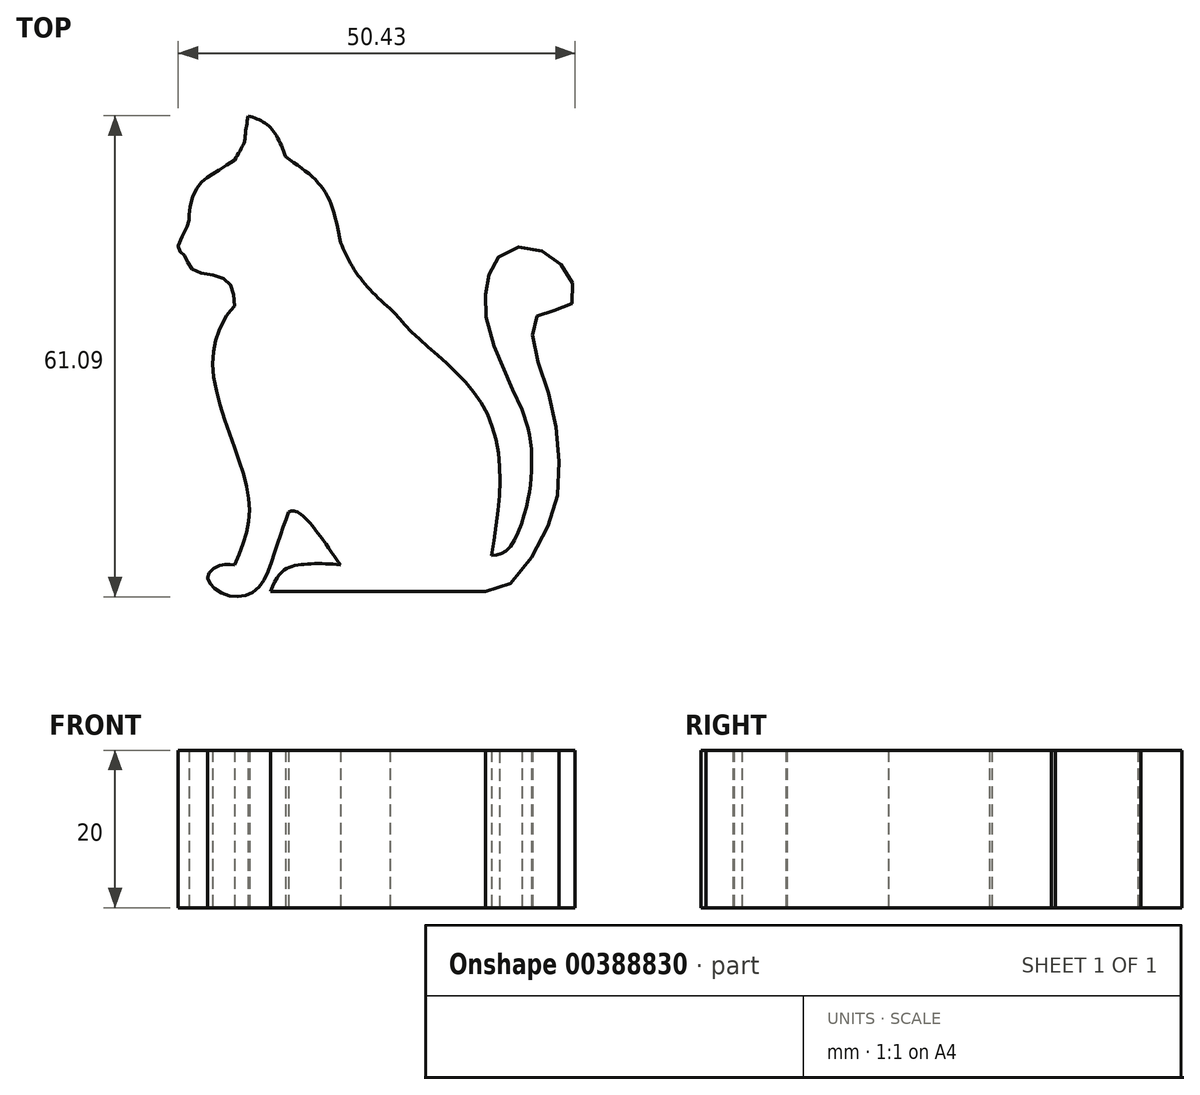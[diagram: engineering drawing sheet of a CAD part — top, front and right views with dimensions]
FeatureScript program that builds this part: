
annotation { "Feature Type Name" : "Feature", "Feature Type Description" : "" }
export const myFeature = defineFeature(function(context is Context, id is Id, definition is map)
    precondition{}
    {
        {
            var Q0;
            Q0=qCreatedBy(makeId("Top.planeOp"),FACE);
            var sketch = newSketch(context, id + "F0", { "sketchPlane" : qUnion([Q0])});
            skFitSpline(sketch, "E0", {"points": [v(-17.16, 28.37) * mm, v(-17.53, 25.84) * mm, v(-17.62, 25.13) * mm, v(-18.9, 22.75) * mm], "startDerivative": vector(-1.28, -7.63) * mm, "endDerivative": vector(-4.15, -6.95) * mm});
            skFitSpline(sketch, "E1", {"points": [v(-18.9, 22.75) * mm, v(-21.25, 21.24) * mm, v(-22.64, 20.3) * mm, v(-24.03, 18.5) * mm, v(-24.68, 15.66) * mm, v(-24.8, 14.64) * mm, v(-26.05, 11.46) * mm, v(-25.25, 10.67) * mm, v(-24.23, 8.85) * mm, v(-20.03, 7.6) * mm, v(-18.9, 4.2) * mm], "startDerivative": vector(-23.37, -15.12) * mm, "endDerivative": vector(1.87, -33.89) * mm});
            skFitSpline(sketch, "E2", {"points": [v(-18.9, 4.2) * mm, v(-20.2, 2.45) * mm, v(-21.65, -3.17) * mm, v(-18.9, -13.76) * mm, v(-17, -22.1) * mm, v(-18.9, -28.7) * mm], "startDerivative": vector(-11.23, -12.61) * mm, "endDerivative": vector(-13.18, -31.36) * mm});
            skFitSpline(sketch, "E3", {"points": [v(-18.9, -28.7) * mm, v(-20.53, -28.7) * mm, v(-22.3, -30.14) * mm, v(-20.2, -32.38) * mm, v(-16.2, -31.9) * mm, v(-13.62, -26.54) * mm, v(-12.02, -21.95) * mm], "startDerivative": vector(-13.16, 2.23) * mm, "endDerivative": vector(8.03, 21.7) * mm});
            skFitSpline(sketch, "E4", {"points": [v(-12.02, -21.95) * mm, v(-10.9, -21.95) * mm, v(-5.44, -28.7) * mm], "startDerivative": vector(3.83, 1.21) * mm, "endDerivative": vector(8.6, -12.54) * mm});
            skFitSpline(sketch, "E5", {"points": [v(-5.44, -28.7) * mm, v(-10.73, -28.7) * mm, v(-14.34, -32.08) * mm], "startDerivative": vector(-10.81, 1.41) * mm, "endDerivative": vector(-6.33, -16.88) * mm});
            skLineSegment(sketch, "E6", {"start": v(-14.34, -32.08) * mm, "end": v(13.02, -32.08) * mm});
            skFitSpline(sketch, "E7", {"points": [v(13.02, -32.08) * mm, v(16.43, -30.83) * mm, v(20.08, -25.5) * mm, v(22.03, -20.3) * mm, v(22.24, -14.16) * mm, v(21.3, -7.88) * mm, v(19.47, -2.34) * mm, v(18.95, 1.15) * mm, v(19.57, 2.92) * mm, v(21.05, 3.54) * mm, v(23.05, 3.92) * mm, v(24.34, 5.2) * mm, v(23.72, 7.83) * mm, v(22.33, 9.74) * mm, v(19.76, 11.36) * mm, v(16.85, 11.65) * mm, v(14.5, 10.31) * mm, v(13.55, 8.45) * mm, v(13.02, 6.54) * mm, v(13.02, 3.63) * mm, v(13.4, 0.86) * mm, v(17.13, -7.96) * mm, v(17.65, -8.92) * mm], "startDerivative": vector(74, 13.03) * mm, "endDerivative": vector(24.57, -12.59) * mm});
            skFitSpline(sketch, "E8", {"points": [v(17.65, -8.92) * mm, v(18.65, -12.53) * mm, v(18.8, -17.03) * mm, v(18.16, -21.36) * mm, v(15.87, -26.7) * mm, v(13.78, -27.5) * mm], "startDerivative": vector(6.18, -17.96) * mm, "endDerivative": vector(-14.64, -1.8) * mm});
            skFitSpline(sketch, "E9", {"points": [v(-17.16, 28.37) * mm, v(-14.4, 26.98) * mm, v(-12.4, 23.17) * mm], "startDerivative": vector(6.56, -2.1) * mm, "endDerivative": vector(3.07, -8.14) * mm});
            skFitSpline(sketch, "E10", {"points": [v(-12.4, 23.17) * mm, v(-8.67, 20.3) * mm, v(-6.67, 17.25) * mm, v(-5.43, 12.29) * mm], "startDerivative": vector(11.88, -8.13) * mm, "endDerivative": vector(2.85, -14.88) * mm});
            skFitSpline(sketch, "E11", {"points": [v(-5.43, 12.29) * mm, v(-3.23, 8.18) * mm, v(0.85, 3.87) * mm], "startDerivative": vector(3.9, -8.96) * mm, "endDerivative": vector(8.9, -7.61) * mm});
            skFitSpline(sketch, "E12", {"points": [v(0.85, 3.87) * mm, v(2.6, 1.97) * mm, v(6.95, -2.1) * mm, v(12.49, -8.12) * mm, v(14.81, -16.63) * mm, v(13.78, -27.5) * mm], "startDerivative": vector(13.95, -10.46) * mm, "endDerivative": vector(-6.96, -44.16) * mm});
            skSolve(sketch);
        }
        {
            var Q0;
            Q0 = qSketchRegion(id + "F0", true);
            extrude(context, id + "F1", {"entities" : qUnion([Q0]), "depth" : 20 * mm});
        }
    });
